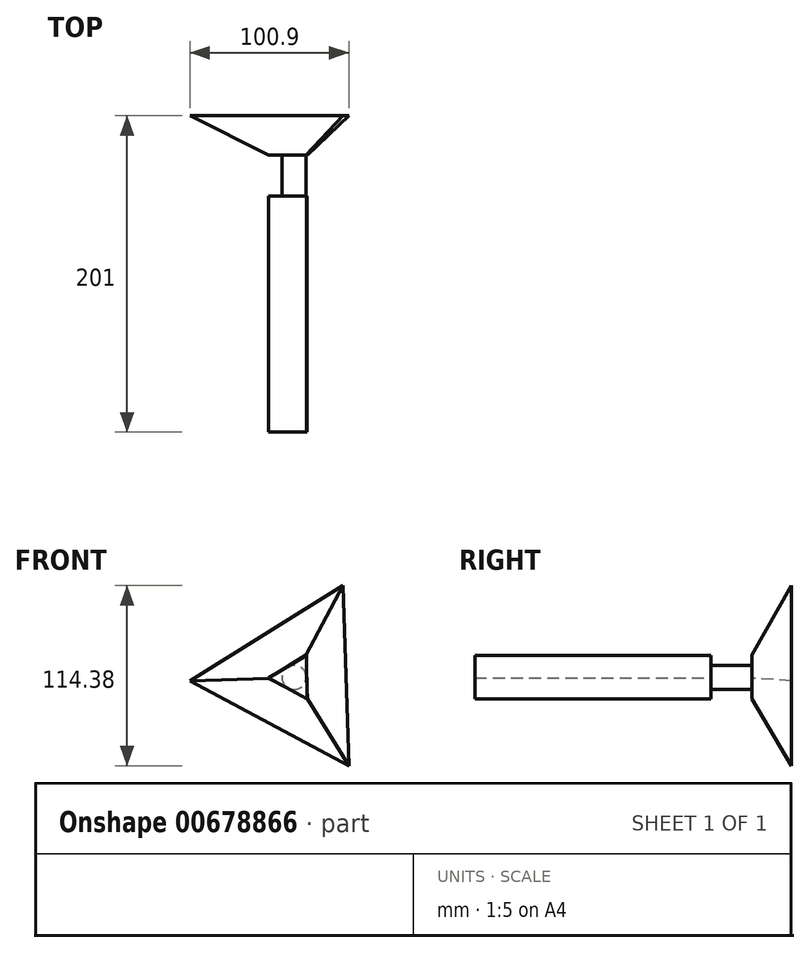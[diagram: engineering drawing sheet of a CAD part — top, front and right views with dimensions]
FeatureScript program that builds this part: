
annotation { "Feature Type Name" : "Feature", "Feature Type Description" : "" }
export const myFeature = defineFeature(function(context is Context, id is Id, definition is map)
    precondition{}
    {
        {
            var Q0;
            Q0=qCreatedBy(makeId("Front.planeOp"),FACE);
            var sketch = newSketch(context, id + "F0", { "sketchPlane" : qUnion([Q0])});
            skLineSegment(sketch, "E0.0", {"start": v(-16.07, -0.25) * mm, "end": v(7.82, 14.04) * mm});
            skLineSegment(sketch, "E0.1", {"start": v(7.82, 14.04) * mm, "end": v(8.25, -13.8) * mm});
            skLineSegment(sketch, "E0.2", {"start": v(8.25, -13.8) * mm, "end": v(-16.07, -0.25) * mm});
            skSolve(sketch);
        }
        {
            var Q0;
            Q0=makeQuery(id+"F0.imprint","IMPRINT",FACE,{"disambiguationData":[TD([[makeQuery(id+"F0.imprint","IMPRINT",EDGE,{"derivedFrom":sQuery(id+"F0.wireOp",EDGE,"E0.0")}),-1.0]])]});
            extrude(context, id + "F1", {"entities" : qUnion([Q0]), "depth" : 150 * mm, "offsetDistance" : 25 * mm});
        }
        {
            var Q0;
            Q0=qCreatedBy(makeId("Front.planeOp"),FACE);
            var sketch = newSketch(context, id + "F2", { "sketchPlane" : qUnion([Q0])});
            skCircle(sketch, "E1", {"center": v(0, 0) * mm, "radius": 7.76 * mm});
            skSolve(sketch);
        }
        {
            var Q0;
            Q0=makeQuery(id+"F2.imprint","IMPRINT",FACE,{"disambiguationData":[TD([[makeQuery(id+"F2.imprint","IMPRINT",EDGE,{"derivedFrom":sQuery(id+"F2.wireOp",EDGE,"E1")}),1.0]])]});
            extrude(context, id + "F3", {"entities" : qUnion([Q0]), "operationType" : NewBodyOperationType.ADD, "oppositeDirection" : true, "depth" : 26 * mm, "offsetDistance" : 25 * mm});
        }
        {
            var Q0;
            Q0=makeQuery(id+"F3.opExtrude","CAP_FACE",FACE,{"disambiguationData":[OSD([sQuery(id+"F2.wireOp",EDGE,"E1")])],"isStart":false});
            var sketch = newSketch(context, id + "F4", { "sketchPlane" : qUnion([Q0])});
            skCircle(sketch, "E2.cCircle", {"center": v(0, 0) * mm, "radius": 8.04 * mm, "construction": true});
            skLineSegment(sketch, "E2.0", {"start": v(-8.48, -13.65) * mm, "end": v(-7.58, 14.17) * mm});
            skLineSegment(sketch, "E2.1", {"start": v(-7.58, 14.17) * mm, "end": v(16.06, -0.52) * mm});
            skLineSegment(sketch, "E2.2", {"start": v(16.06, -0.52) * mm, "end": v(-8.48, -13.65) * mm});
            skPoint(sketch, "E2.0.midPoint", {"position": v(-8.03, 0.26) * mm});
            skSolve(sketch);
        }
        {
            var Q0;
            Q0 = qSketchRegion(id + "F4", true);
            extrude(context, id + "F5", {"entities" : qUnion([Q0]), "operationType" : NewBodyOperationType.ADD, "depth" : 25 * mm, "offsetDistance" : 25 * mm, "hasDraft" : true, "draftAngle" : 45 * degree});
        }
    });
